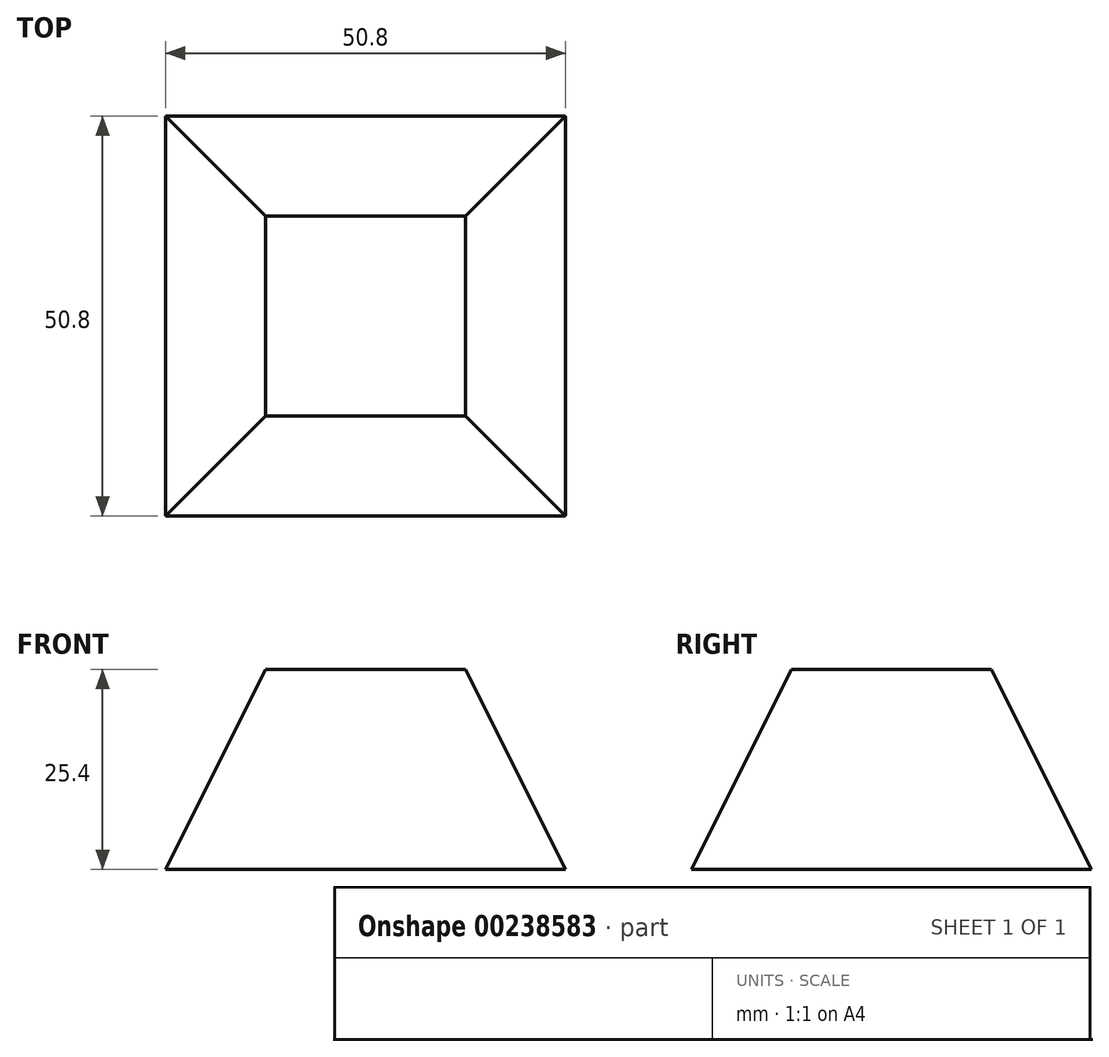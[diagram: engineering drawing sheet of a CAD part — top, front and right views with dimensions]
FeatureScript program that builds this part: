
annotation { "Feature Type Name" : "Feature", "Feature Type Description" : "" }
export const myFeature = defineFeature(function(context is Context, id is Id, definition is map)
    precondition{}
    {
        {
            var Q0;
            Q0=qCreatedBy(makeId("Top.planeOp"),FACE);
            var sketch = newSketch(context, id + "F0", { "sketchPlane" : qUnion([Q0])});
            skLineSegment(sketch, "E0.bottom", {"start": v(0, 0) * mm, "end": v(50.8, 0) * mm});
            skLineSegment(sketch, "E0.top", {"start": v(0, 50.8) * mm, "end": v(50.8, 50.8) * mm});
            skLineSegment(sketch, "E0.left", {"start": v(0, 0) * mm, "end": v(0, 50.8) * mm});
            skLineSegment(sketch, "E0.right", {"start": v(50.8, 0) * mm, "end": v(50.8, 50.8) * mm});
            skSolve(sketch);
        }
        {
            var Q0;
            Q0=qCreatedBy(makeId("Top.planeOp"),FACE);
            cPlane(context, id + "F1", {"entities" : qUnion([Q0]), "cplaneType" : CPlaneType.OFFSET, "offset" : 25.4 * mm, "width" : 152.4 * mm, "height" : 152.4 * mm});
        }
        {
            var Q0;
            Q0=qCreatedBy(id+"F1.planeOp",FACE);
            var sketch = newSketch(context, id + "F2", { "sketchPlane" : qUnion([Q0])});
            skLineSegment(sketch, "E1.0.0", {"start": v(50.8, 50.8) * mm, "end": v(0, 50.8) * mm, "construction": true});
            skLineSegment(sketch, "E1.0.1", {"start": v(0, 50.8) * mm, "end": v(0, 0) * mm, "construction": true});
            skLineSegment(sketch, "E1.0.2", {"start": v(0, 0) * mm, "end": v(50.8, 0) * mm, "construction": true});
            skLineSegment(sketch, "E1.0.3", {"start": v(50.8, 0) * mm, "end": v(50.8, 50.8) * mm, "construction": true});
            skPoint(sketch, "E2", {"position": v(12.7, 12.7) * mm});
            skPoint(sketch, "E3", {"position": v(12.7, 38.1) * mm});
            skPoint(sketch, "E4", {"position": v(38.1, 38.1) * mm});
            skPoint(sketch, "E5", {"position": v(38.1, 12.7) * mm});
            skLineSegment(sketch, "E6", {"start": v(12.7, 12.7) * mm, "end": v(38.1, 12.7) * mm});
            skLineSegment(sketch, "E7", {"start": v(38.1, 38.1) * mm, "end": v(38.1, 12.7) * mm});
            skLineSegment(sketch, "E8", {"start": v(38.1, 38.1) * mm, "end": v(12.7, 38.1) * mm});
            skLineSegment(sketch, "E9", {"start": v(12.7, 38.1) * mm, "end": v(12.7, 12.7) * mm});
            skSolve(sketch);
        }
        {
            var Q0;
            Q0=makeQuery(id+"F0.imprint","IMPRINT",FACE,{"disambiguationData":[TD([[makeQuery(id+"F0.imprint","IMPRINT",EDGE,{"derivedFrom":sQuery(id+"F0.wireOp",EDGE,"E0.bottom")}),1.0]])]});
            var Q1;
            Q1=makeQuery(id+"F2.imprint","IMPRINT",FACE,{"disambiguationData":[TD([[makeQuery(id+"F2.imprint","IMPRINT",EDGE,{"derivedFrom":sQuery(id+"F2.wireOp",EDGE,"E6")}),1.0]])]});
            loft(context, id + "F3", {"sheetProfilesArray" : [{ "sheetProfileEntities" : qUnion([Q0]) }, { "sheetProfileEntities" : qUnion([Q1]) }]});
        }
    });
